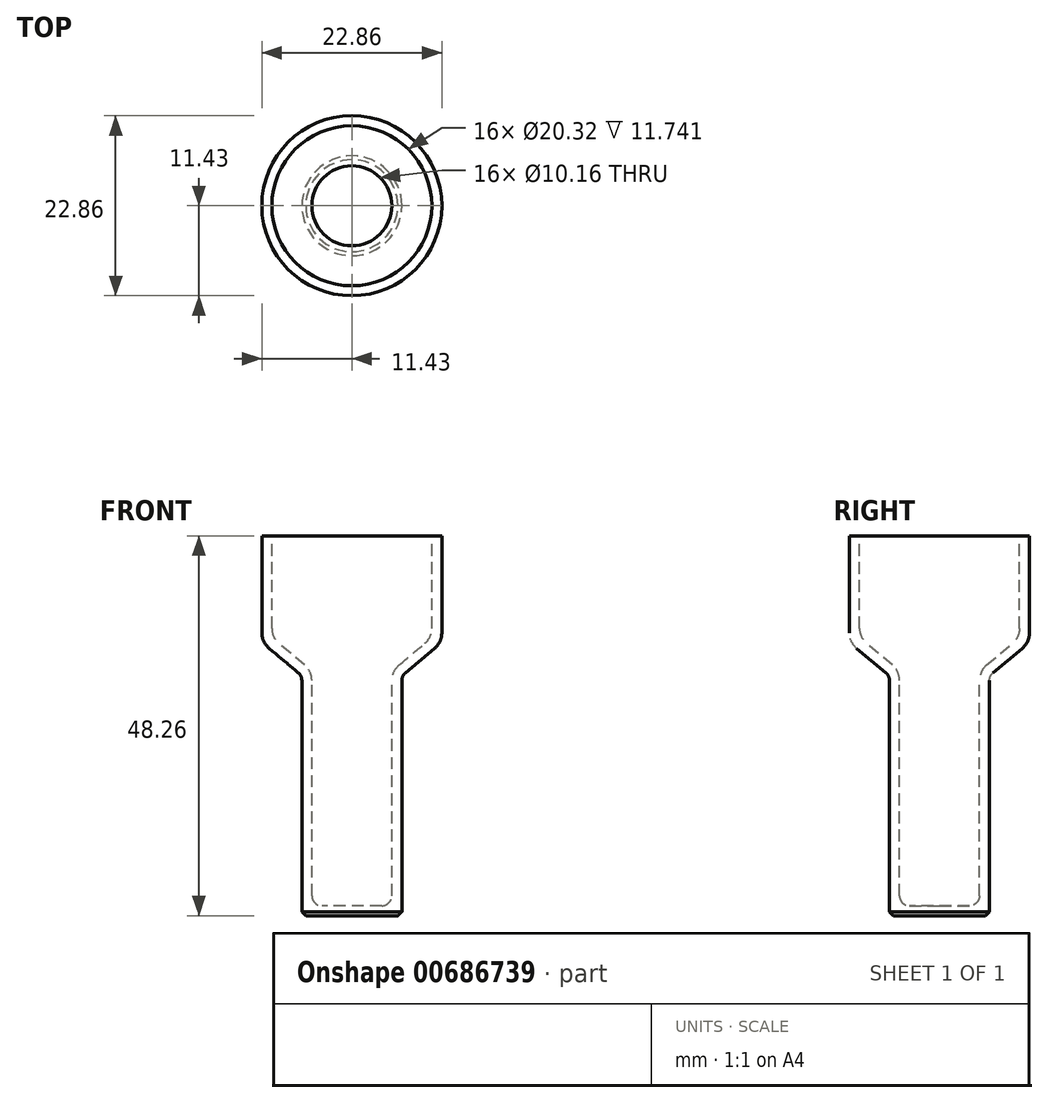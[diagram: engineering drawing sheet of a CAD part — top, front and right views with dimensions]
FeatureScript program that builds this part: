
annotation { "Feature Type Name" : "Feature", "Feature Type Description" : "" }
export const myFeature = defineFeature(function(context is Context, id is Id, definition is map)
    precondition{}
    {
        {
            var Q0;
            Q0=qCreatedBy(makeId("Front.planeOp"),FACE);
            var sketch = newSketch(context, id + "F0", { "sketchPlane" : qUnion([Q0])});
            skLineSegment(sketch, "E0", {"start": v(6.35, -5.88) * mm, "end": v(6.35, 19.5) * mm, "construction": true});
            skLineSegment(sketch, "E1.right", {"start": v(6.35, 30.48) * mm, "end": v(6.35, 0) * mm});
            skLineSegment(sketch, "E2.top", {"start": v(0, 1.27) * mm, "end": v(5.08, 1.27) * mm});
            skLineSegment(sketch, "E2.left", {"start": v(0, 0) * mm, "end": v(0, 1.27) * mm});
            skLineSegment(sketch, "E3", {"start": v(5.08, 31.07) * mm, "end": v(5.08, 1.27) * mm});
            skLineSegment(sketch, "E4", {"start": v(0, 0) * mm, "end": v(6.35, 0) * mm});
            skLineSegment(sketch, "E5", {"start": v(0, 48.79) * mm, "end": v(0, -8.85) * mm, "construction": true});
            skLineSegment(sketch, "E6", {"start": v(6.35, 30.48) * mm, "end": v(11.43, 34.74) * mm});
            skLineSegment(sketch, "E7", {"start": v(11.43, 34.74) * mm, "end": v(11.43, 48.26) * mm});
            skLineSegment(sketch, "E8", {"start": v(11.43, 48.26) * mm, "end": v(10.16, 48.26) * mm});
            skLineSegment(sketch, "E9", {"start": v(10.16, 48.26) * mm, "end": v(10.16, 35.33) * mm});
            skLineSegment(sketch, "E10", {"start": v(10.16, 35.33) * mm, "end": v(5.08, 31.07) * mm});
            skLineSegment(sketch, "E11", {"start": v(6.35, 30.48) * mm, "end": v(25.54, 30.48) * mm, "construction": true});
            skSolve(sketch);
        }
        {
            var Q0;
            Q0=makeQuery(id+"F0.imprint","IMPRINT",FACE,{"disambiguationData":[TD([[makeQuery(id+"F0.imprint","IMPRINT",EDGE,{"derivedFrom":sQuery(id+"F0.wireOp",EDGE,"E1.right")}),-1.0]])]});
            var Q1;
            Q1=sQuery(id+"F0.wireOp",EDGE,"E5");
            revolve(context, id + "F1", {"entities" : qUnion([Q0]), "axis" : qUnion([Q1]), "revolveType" : RevolveType.FULL});
        }
        {
            var Q0;
            Q0=makeQuery(id+"F1.opRevolve","SWEPT_EDGE",EDGE,{"disambiguationData":[OSD([sQuery(id+"F0.wireOp",EDGE,"E2.top"),sQuery(id+"F0.wireOp",EDGE,"E3")])]});
            fillet(context, id + "F2", {"entities" : qUnion([Q0]), "radius" : 1.27 * mm, "tangentPropagation" : true, "allowEdgeOverflow" : false});
        }
        {
            var Q0;
            Q0=makeQuery(id+"F1.opRevolve","SWEPT_EDGE",EDGE,{"disambiguationData":[OSD([sQuery(id+"F0.wireOp",EDGE,"E1.right"),sQuery(id+"F0.wireOp",EDGE,"E4")])]});
            chamfer(context, id + "F3", {"entities" : qUnion([Q0]), "width" : 0.5 * mm, "tangentPropagation" : true});
        }
        {
            var Q0;
            Q0=makeQuery(id+"F1.opRevolve","SWEPT_EDGE",EDGE,{"disambiguationData":[OSD([sQuery(id+"F0.wireOp",EDGE,"E1.right"),sQuery(id+"F0.wireOp",EDGE,"E6")])]});
            fillet(context, id + "F4", {"entities" : qUnion([Q0]), "radius" : 1.27 * mm, "tangentPropagation" : true, "allowEdgeOverflow" : false});
        }
        {
            var Q0;
            Q0=makeQuery(id+"F1.opRevolve","SWEPT_EDGE",EDGE,{"disambiguationData":[OSD([sQuery(id+"F0.wireOp",EDGE,"E6"),sQuery(id+"F0.wireOp",EDGE,"E7")])]});
            fillet(context, id + "F5", {"entities" : qUnion([Q0]), "radius" : 2.54 * mm, "tangentPropagation" : true, "allowEdgeOverflow" : false});
        }
        {
            var Q0;
            Q0=makeQuery(id+"F1.opRevolve","SWEPT_EDGE",EDGE,{"disambiguationData":[OSD([sQuery(id+"F0.wireOp",EDGE,"E9"),sQuery(id+"F0.wireOp",EDGE,"E10")])]});
            var Q1;
            Q1=makeQuery(id+"F1.opRevolve","SWEPT_EDGE",EDGE,{"disambiguationData":[OSD([sQuery(id+"F0.wireOp",EDGE,"E3"),sQuery(id+"F0.wireOp",EDGE,"E10")])]});
            fillet(context, id + "F6", {"entities" : qUnion([Q0, Q1]), "radius" : 2.54 * mm, "tangentPropagation" : true, "allowEdgeOverflow" : false});
        }
        {
            var Q0;
            Q0=makeQuery(id+"F1.opRevolve","SWEPT_BODY",BODY,{"disambiguationData":[OSD([sQuery(id+"F0.wireOp",EDGE,"E1.right"),sQuery(id+"F0.wireOp",EDGE,"E2.top"),sQuery(id+"F0.wireOp",EDGE,"E2.left"),sQuery(id+"F0.wireOp",EDGE,"E3"),sQuery(id+"F0.wireOp",EDGE,"E4"),sQuery(id+"F0.wireOp",EDGE,"E6"),sQuery(id+"F0.wireOp",EDGE,"E7"),sQuery(id+"F0.wireOp",EDGE,"E8"),sQuery(id+"F0.wireOp",EDGE,"E9"),sQuery(id+"F0.wireOp",EDGE,"E10")])]});
            transform(context, id + "F7", {"entities" : qUnion([Q0]), "transformType" : TransformType.TRANSLATION_3D, "dx" : 69.85 * mm, "dy" : 0 * mm, "dz" : 0 * mm, "makeCopy" : true});
        }
        {
            var Q0;
            Q0=makeQuery(id+"F7.opPattern","COPY",BODY,{"derivedFrom":makeQuery(id+"F1.opRevolve","SWEPT_BODY",BODY,{"disambiguationData":[OSD([sQuery(id+"F0.wireOp",EDGE,"E1.right"),sQuery(id+"F0.wireOp",EDGE,"E2.top"),sQuery(id+"F0.wireOp",EDGE,"E2.left"),sQuery(id+"F0.wireOp",EDGE,"E3"),sQuery(id+"F0.wireOp",EDGE,"E4"),sQuery(id+"F0.wireOp",EDGE,"E6"),sQuery(id+"F0.wireOp",EDGE,"E7"),sQuery(id+"F0.wireOp",EDGE,"E8"),sQuery(id+"F0.wireOp",EDGE,"E9"),sQuery(id+"F0.wireOp",EDGE,"E10")])]}),"instanceName":"1"});
            deleteBodies(context, id + "F8", {"entities" : qUnion([Q0])});
        }
    });
